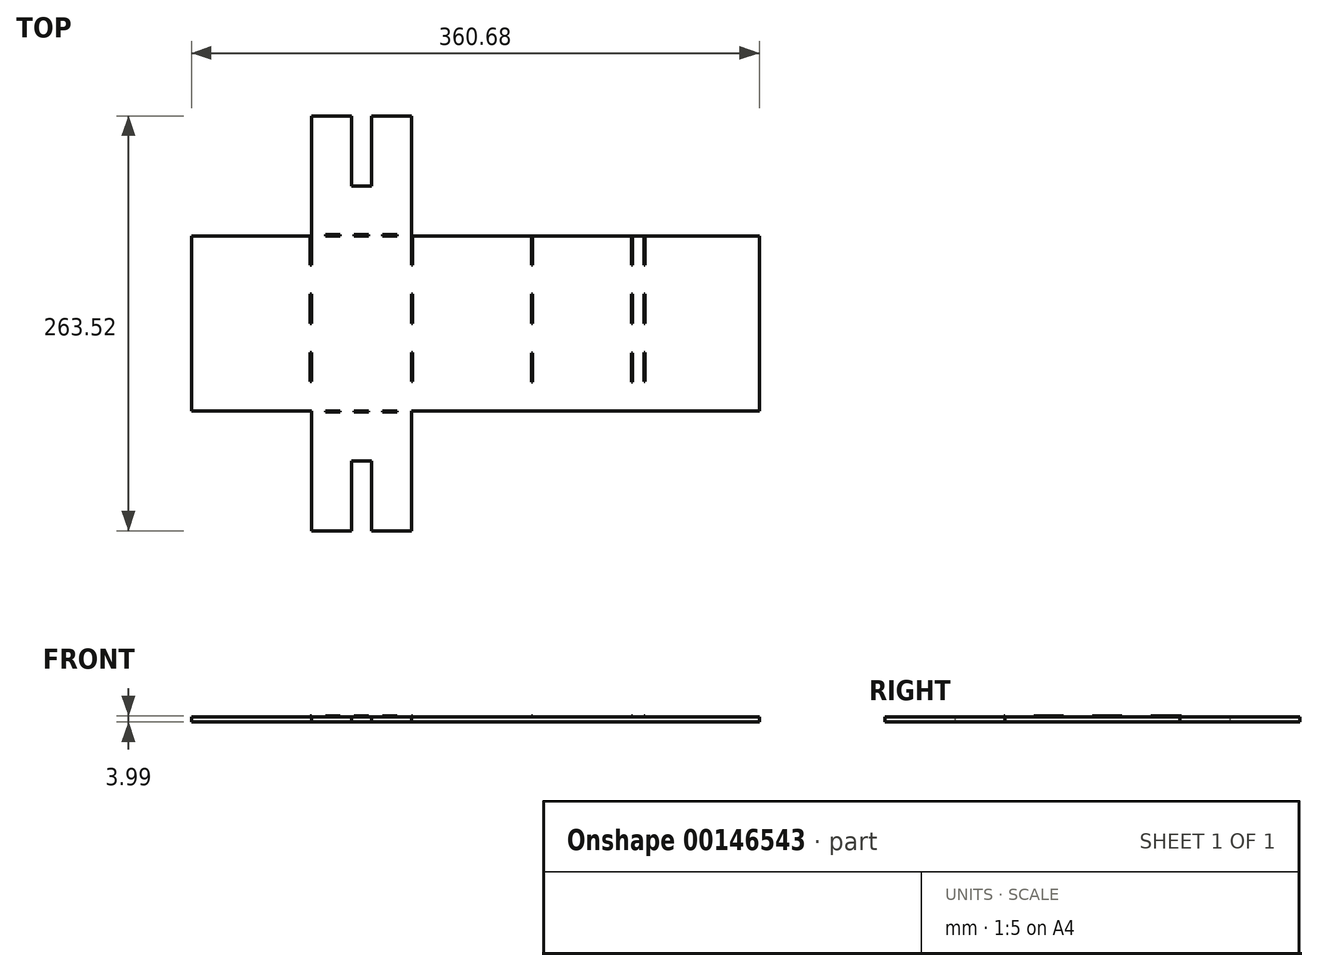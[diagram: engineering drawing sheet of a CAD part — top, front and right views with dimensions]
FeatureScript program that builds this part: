
annotation { "Feature Type Name" : "Feature", "Feature Type Description" : "" }
export const myFeature = defineFeature(function(context is Context, id is Id, definition is map)
    precondition{}
    {
        {
            var Q0;
            Q0=qCreatedBy(makeId("Top.planeOp"),FACE);
            var sketch = newSketch(context, id + "F0", { "sketchPlane" : qUnion([Q0])});
            skLineSegment(sketch, "E0", {"start": v(0, 187.33) * mm, "end": v(-25.4, 187.33) * mm});
            skLineSegment(sketch, "E1", {"start": v(-63.5, 187.33) * mm, "end": v(-63.5, 111.13) * mm});
            skLineSegment(sketch, "E2", {"start": v(-63.5, -76.2) * mm, "end": v(-38.1, -76.2) * mm});
            skLineSegment(sketch, "E3", {"start": v(0, -76.2) * mm, "end": v(0, 0) * mm});
            skLineSegment(sketch, "E4", {"start": v(0, 0) * mm, "end": v(220.98, 0) * mm});
            skLineSegment(sketch, "E5", {"start": v(220.98, 0) * mm, "end": v(220.98, 111.13) * mm});
            skLineSegment(sketch, "E6", {"start": v(220.98, 111.13) * mm, "end": v(0, 111.12) * mm});
            skLineSegment(sketch, "E7", {"start": v(0, 111.13) * mm, "end": v(0, 187.33) * mm});
            skLineSegment(sketch, "E8", {"start": v(-63.5, 111.13) * mm, "end": v(-139.7, 111.13) * mm});
            skLineSegment(sketch, "E9", {"start": v(-139.7, 111.13) * mm, "end": v(-139.7, 0) * mm});
            skLineSegment(sketch, "E10", {"start": v(-139.7, 0) * mm, "end": v(-63.5, 0) * mm});
            skLineSegment(sketch, "E11.trimOffspring", {"start": v(-63.5, 0) * mm, "end": v(-63.5, -76.2) * mm});
            skLineSegment(sketch, "E12", {"start": v(-38.1, 187.33) * mm, "end": v(-38.1, 142.88) * mm});
            skLineSegment(sketch, "E13", {"start": v(-38.1, 142.88) * mm, "end": v(-25.4, 142.88) * mm});
            skLineSegment(sketch, "E14", {"start": v(-25.4, 142.88) * mm, "end": v(-25.4, 187.33) * mm});
            skLineSegment(sketch, "E15", {"start": v(-25.4, -76.2) * mm, "end": v(-25.4, -31.75) * mm});
            skLineSegment(sketch, "E16", {"start": v(-25.4, -31.75) * mm, "end": v(-38.1, -31.75) * mm});
            skLineSegment(sketch, "E17", {"start": v(-38.1, -31.75) * mm, "end": v(-38.1, -76.2) * mm});
            skLineSegment(sketch, "E18.trimOffspring", {"start": v(-38.1, 187.33) * mm, "end": v(-63.5, 187.33) * mm});
            skLineSegment(sketch, "E19.trimOffspring", {"start": v(-25.4, -76.2) * mm, "end": v(0, -76.2) * mm});
            skSolve(sketch);
        }
        {
            var Q0;
            Q0 = qSketchRegion(id + "F0", true);
            extrude(context, id + "F1", {"entities" : qUnion([Q0]), "depth" : 3.17 * mm});
        }
        {
            var Q0;
            Q0=makeQuery(id+"F1.opExtrude","CAP_FACE",FACE,{"disambiguationData":[OSD([sQuery(id+"F0.wireOp",EDGE,"E0"),sQuery(id+"F0.wireOp",EDGE,"E1"),sQuery(id+"F0.wireOp",EDGE,"E2"),sQuery(id+"F0.wireOp",EDGE,"E3"),sQuery(id+"F0.wireOp",EDGE,"E4"),sQuery(id+"F0.wireOp",EDGE,"E5"),sQuery(id+"F0.wireOp",EDGE,"E6"),sQuery(id+"F0.wireOp",EDGE,"E7"),sQuery(id+"F0.wireOp",EDGE,"E8"),sQuery(id+"F0.wireOp",EDGE,"E9"),sQuery(id+"F0.wireOp",EDGE,"E10"),sQuery(id+"F0.wireOp",EDGE,"E11.trimOffspring")])],"isStart":false});
            var sketch = newSketch(context, id + "F2", { "sketchPlane" : qUnion([Q0])});
            skLineSegment(sketch, "E20", {"start": v(-63.5, 111.13) * mm, "end": v(-63.5, 92.6) * mm});
            skLineSegment(sketch, "E21", {"start": v(-63.5, 74.08) * mm, "end": v(-63.5, 55.56) * mm});
            skLineSegment(sketch, "E22", {"start": v(-63.5, 37.04) * mm, "end": v(-63.5, 18.52) * mm});
            skLineSegment(sketch, "E23", {"start": v(-63.5, 18.52) * mm, "end": v(-64.31, 18.52) * mm});
            skLineSegment(sketch, "E24", {"start": v(-64.31, 18.52) * mm, "end": v(-64.31, 37.04) * mm});
            skLineSegment(sketch, "E25", {"start": v(-64.31, 37.04) * mm, "end": v(-63.5, 37.04) * mm});
            skLineSegment(sketch, "E26", {"start": v(-63.5, 55.56) * mm, "end": v(-64.31, 55.56) * mm});
            skLineSegment(sketch, "E27", {"start": v(-64.31, 55.56) * mm, "end": v(-64.31, 74.08) * mm});
            skLineSegment(sketch, "E28", {"start": v(-64.31, 74.08) * mm, "end": v(-63.5, 74.08) * mm});
            skLineSegment(sketch, "E29", {"start": v(-63.5, 92.6) * mm, "end": v(-64.31, 92.6) * mm});
            skLineSegment(sketch, "E30", {"start": v(-64.31, 92.6) * mm, "end": v(-64.31, 111.13) * mm});
            skLineSegment(sketch, "E31", {"start": v(-64.31, 111.13) * mm, "end": v(-63.5, 111.13) * mm});
            skLineSegment(sketch, "E32", {"start": v(-63.5, 92.6) * mm, "end": v(-63.5, 74.08) * mm, "construction": true});
            skLineSegment(sketch, "E33", {"start": v(-63.5, 55.56) * mm, "end": v(-63.5, 37.04) * mm, "construction": true});
            skLineSegment(sketch, "E34", {"start": v(-63.5, 0) * mm, "end": v(-63.5, 18.52) * mm, "construction": true});
            skLineSegment(sketch, "E35.1.0.0", {"start": v(0.81, 18.52) * mm, "end": v(0, 18.52) * mm});
            skLineSegment(sketch, "E35.1.0.1", {"start": v(0, 18.52) * mm, "end": v(0, 37.04) * mm});
            skLineSegment(sketch, "E35.1.0.2", {"start": v(0.81, 37.04) * mm, "end": v(0.81, 18.52) * mm});
            skLineSegment(sketch, "E35.1.0.3", {"start": v(0, 37.04) * mm, "end": v(0.81, 37.04) * mm});
            skLineSegment(sketch, "E35.1.0.4", {"start": v(0.81, 55.56) * mm, "end": v(0, 55.56) * mm});
            skLineSegment(sketch, "E35.1.0.5", {"start": v(0, 55.56) * mm, "end": v(0, 74.08) * mm});
            skLineSegment(sketch, "E35.1.0.6", {"start": v(0.81, 74.08) * mm, "end": v(0.81, 55.56) * mm});
            skLineSegment(sketch, "E35.1.0.7", {"start": v(0, 74.08) * mm, "end": v(0.81, 74.08) * mm});
            skLineSegment(sketch, "E35.1.0.8", {"start": v(0.81, 92.6) * mm, "end": v(0, 92.6) * mm});
            skLineSegment(sketch, "E35.1.0.9", {"start": v(0, 92.6) * mm, "end": v(0, 111.13) * mm});
            skLineSegment(sketch, "E35.1.0.10", {"start": v(0.81, 111.13) * mm, "end": v(0.81, 92.6) * mm});
            skLineSegment(sketch, "E35.1.0.11", {"start": v(0, 111.13) * mm, "end": v(0.81, 111.13) * mm});
            skLineSegment(sketch, "E36.1.0.0", {"start": v(76.2, 92.63) * mm, "end": v(76.2, 111.15) * mm});
            skLineSegment(sketch, "E36.1.0.1", {"start": v(77.01, 111.15) * mm, "end": v(77.01, 92.63) * mm});
            skLineSegment(sketch, "E36.1.0.2", {"start": v(76.2, 111.15) * mm, "end": v(77.01, 111.15) * mm});
            skLineSegment(sketch, "E36.1.0.3", {"start": v(77.01, 92.63) * mm, "end": v(76.2, 92.63) * mm});
            skLineSegment(sketch, "E36.1.0.4", {"start": v(77.01, 74.1) * mm, "end": v(77.01, 55.59) * mm});
            skLineSegment(sketch, "E36.1.0.5", {"start": v(76.2, 55.59) * mm, "end": v(76.2, 74.1) * mm});
            skLineSegment(sketch, "E36.1.0.6", {"start": v(76.2, 74.1) * mm, "end": v(77.01, 74.1) * mm});
            skLineSegment(sketch, "E36.1.0.7", {"start": v(77.01, 55.59) * mm, "end": v(76.2, 55.59) * mm});
            skLineSegment(sketch, "E36.1.0.8", {"start": v(77.01, 36.8) * mm, "end": v(77.01, 18.29) * mm});
            skLineSegment(sketch, "E36.1.0.9", {"start": v(76.2, 18.29) * mm, "end": v(76.2, 36.8) * mm});
            skLineSegment(sketch, "E36.1.0.10", {"start": v(76.2, 36.8) * mm, "end": v(77.01, 36.8) * mm});
            skLineSegment(sketch, "E36.1.0.11", {"start": v(77.01, 18.29) * mm, "end": v(76.2, 18.29) * mm});
            skLineSegment(sketch, "E37.1.0.0", {"start": v(139.7, 92.6) * mm, "end": v(139.7, 111.13) * mm});
            skLineSegment(sketch, "E37.1.0.1", {"start": v(139.7, 18.26) * mm, "end": v(139.7, 36.78) * mm});
            skLineSegment(sketch, "E37.1.0.2", {"start": v(139.7, 55.56) * mm, "end": v(139.7, 74.08) * mm});
            skLineSegment(sketch, "E37.1.0.3", {"start": v(140.51, 74.08) * mm, "end": v(140.51, 55.56) * mm});
            skLineSegment(sketch, "E37.1.0.4", {"start": v(140.51, 36.78) * mm, "end": v(140.51, 18.26) * mm});
            skLineSegment(sketch, "E37.1.0.5", {"start": v(140.51, 111.13) * mm, "end": v(140.51, 92.6) * mm});
            skLineSegment(sketch, "E37.1.0.6", {"start": v(139.7, 111.13) * mm, "end": v(140.51, 111.13) * mm});
            skLineSegment(sketch, "E37.1.0.7", {"start": v(140.51, 55.56) * mm, "end": v(139.7, 55.56) * mm});
            skLineSegment(sketch, "E37.1.0.8", {"start": v(139.7, 36.78) * mm, "end": v(140.51, 36.78) * mm});
            skLineSegment(sketch, "E37.1.0.9", {"start": v(139.7, 74.08) * mm, "end": v(140.51, 74.08) * mm});
            skLineSegment(sketch, "E37.1.0.10", {"start": v(140.51, 18.26) * mm, "end": v(139.7, 18.26) * mm});
            skLineSegment(sketch, "E37.1.0.11", {"start": v(140.51, 92.6) * mm, "end": v(139.7, 92.6) * mm});
            skLineSegment(sketch, "E38.1.0.0", {"start": v(147.64, 111.13) * mm, "end": v(148.45, 111.13) * mm});
            skLineSegment(sketch, "E38.1.0.1", {"start": v(147.64, 92.6) * mm, "end": v(147.64, 111.13) * mm});
            skLineSegment(sketch, "E38.1.0.2", {"start": v(148.45, 111.13) * mm, "end": v(148.45, 92.6) * mm});
            skLineSegment(sketch, "E38.1.0.3", {"start": v(148.45, 92.6) * mm, "end": v(147.64, 92.6) * mm});
            skLineSegment(sketch, "E38.1.0.4", {"start": v(148.45, 74.08) * mm, "end": v(148.45, 55.56) * mm});
            skLineSegment(sketch, "E38.1.0.5", {"start": v(147.64, 55.56) * mm, "end": v(147.64, 74.08) * mm});
            skLineSegment(sketch, "E38.1.0.6", {"start": v(148.45, 55.56) * mm, "end": v(147.64, 55.56) * mm});
            skLineSegment(sketch, "E38.1.0.7", {"start": v(147.64, 74.08) * mm, "end": v(148.45, 74.08) * mm});
            skLineSegment(sketch, "E38.1.0.8", {"start": v(147.64, 37.04) * mm, "end": v(148.45, 37.04) * mm});
            skLineSegment(sketch, "E38.1.0.9", {"start": v(148.45, 37.04) * mm, "end": v(148.45, 18.52) * mm});
            skLineSegment(sketch, "E38.1.0.10", {"start": v(147.64, 18.52) * mm, "end": v(147.64, 37.04) * mm});
            skLineSegment(sketch, "E38.1.0.11", {"start": v(148.45, 18.52) * mm, "end": v(147.64, 18.52) * mm});
            skLineSegment(sketch, "E39", {"start": v(-54.43, 0) * mm, "end": v(-45.36, 0) * mm});
            skLineSegment(sketch, "E40", {"start": v(-45.36, 0) * mm, "end": v(-45.36, -0.81) * mm});
            skLineSegment(sketch, "E41", {"start": v(-45.36, -0.81) * mm, "end": v(-54.43, -0.81) * mm});
            skLineSegment(sketch, "E42", {"start": v(-54.43, -0.81) * mm, "end": v(-54.43, 0) * mm});
            skLineSegment(sketch, "E43", {"start": v(-36.29, 0) * mm, "end": v(-36.29, -0.81) * mm});
            skLineSegment(sketch, "E44", {"start": v(-36.29, -0.81) * mm, "end": v(-27.21, -0.81) * mm});
            skLineSegment(sketch, "E45", {"start": v(-27.21, -0.81) * mm, "end": v(-27.21, 0) * mm});
            skLineSegment(sketch, "E46", {"start": v(-27.21, 0) * mm, "end": v(-36.29, 0) * mm});
            skLineSegment(sketch, "E47", {"start": v(-18.14, 0) * mm, "end": v(-18.14, -0.81) * mm});
            skLineSegment(sketch, "E48", {"start": v(-18.14, -0.81) * mm, "end": v(-9.07, -0.81) * mm});
            skLineSegment(sketch, "E49", {"start": v(-9.07, -0.81) * mm, "end": v(-9.07, 0) * mm});
            skLineSegment(sketch, "E50", {"start": v(-9.07, 0) * mm, "end": v(-18.14, 0) * mm});
            skLineSegment(sketch, "E51", {"start": v(-63.5, 0) * mm, "end": v(-54.43, 0) * mm, "construction": true});
            skLineSegment(sketch, "E52", {"start": v(-45.36, 0) * mm, "end": v(-36.29, 0) * mm, "construction": true});
            skLineSegment(sketch, "E53", {"start": v(-27.21, 0) * mm, "end": v(-18.14, 0) * mm, "construction": true});
            skLineSegment(sketch, "E54", {"start": v(0, 0) * mm, "end": v(-9.07, 0) * mm, "construction": true});
            skLineSegment(sketch, "E55.0.1.0", {"start": v(-27.21, 111.94) * mm, "end": v(-36.29, 111.94) * mm});
            skLineSegment(sketch, "E55.0.1.1", {"start": v(-18.14, 111.13) * mm, "end": v(-9.07, 111.13) * mm});
            skLineSegment(sketch, "E55.0.1.2", {"start": v(-54.43, 111.94) * mm, "end": v(-45.36, 111.94) * mm});
            skLineSegment(sketch, "E55.0.1.3", {"start": v(-36.29, 111.13) * mm, "end": v(-27.21, 111.13) * mm});
            skLineSegment(sketch, "E55.0.1.4", {"start": v(-45.36, 111.13) * mm, "end": v(-54.43, 111.13) * mm});
            skLineSegment(sketch, "E55.0.1.5", {"start": v(-9.07, 111.94) * mm, "end": v(-18.14, 111.94) * mm});
            skLineSegment(sketch, "E55.0.1.6", {"start": v(-36.29, 111.94) * mm, "end": v(-36.29, 111.13) * mm});
            skLineSegment(sketch, "E55.0.1.7", {"start": v(-45.36, 111.94) * mm, "end": v(-45.36, 111.13) * mm});
            skLineSegment(sketch, "E55.0.1.8", {"start": v(-27.21, 111.13) * mm, "end": v(-27.21, 111.94) * mm});
            skLineSegment(sketch, "E55.0.1.9", {"start": v(-54.43, 111.13) * mm, "end": v(-54.43, 111.94) * mm});
            skLineSegment(sketch, "E55.0.1.10", {"start": v(-9.07, 111.13) * mm, "end": v(-9.07, 111.94) * mm});
            skLineSegment(sketch, "E55.0.1.11", {"start": v(-18.14, 111.94) * mm, "end": v(-18.14, 111.13) * mm});
            skLineSegment(sketch, "E56", {"start": v(0.81, 92.6) * mm, "end": v(0.81, 74.08) * mm, "construction": true});
            skLineSegment(sketch, "E57", {"start": v(0.81, 37.04) * mm, "end": v(0.81, 55.56) * mm, "construction": true});
            skLineSegment(sketch, "E58", {"start": v(0.81, 18.52) * mm, "end": v(0.81, 0) * mm, "construction": true});
            skLineSegment(sketch, "E59", {"start": v(76.2, 18.29) * mm, "end": v(76.2, 0) * mm, "construction": true});
            skLineSegment(sketch, "E60", {"start": v(76.2, 36.8) * mm, "end": v(76.2, 55.59) * mm, "construction": true});
            skLineSegment(sketch, "E61", {"start": v(76.2, 74.1) * mm, "end": v(76.2, 92.63) * mm, "construction": true});
            skLineSegment(sketch, "E62", {"start": v(139.7, 18.26) * mm, "end": v(139.7, 0) * mm, "construction": true});
            skLineSegment(sketch, "E63", {"start": v(139.7, 55.56) * mm, "end": v(139.7, 36.78) * mm, "construction": true});
            skLineSegment(sketch, "E64", {"start": v(139.7, 92.6) * mm, "end": v(139.7, 74.08) * mm, "construction": true});
            skLineSegment(sketch, "E65", {"start": v(147.64, 92.6) * mm, "end": v(147.64, 74.08) * mm, "construction": true});
            skLineSegment(sketch, "E66", {"start": v(147.64, 55.56) * mm, "end": v(147.64, 37.04) * mm, "construction": true});
            skLineSegment(sketch, "E67", {"start": v(147.64, 18.52) * mm, "end": v(147.64, 0) * mm, "construction": true});
            skSolve(sketch);
        }
        {
            var Q0;
            Q0 = qSketchRegion(id + "F2", true);
            extrude(context, id + "F3", {"entities" : qUnion([Q0]), "operationType" : NewBodyOperationType.ADD, "depth" : 0.81 * mm});
        }
    });
